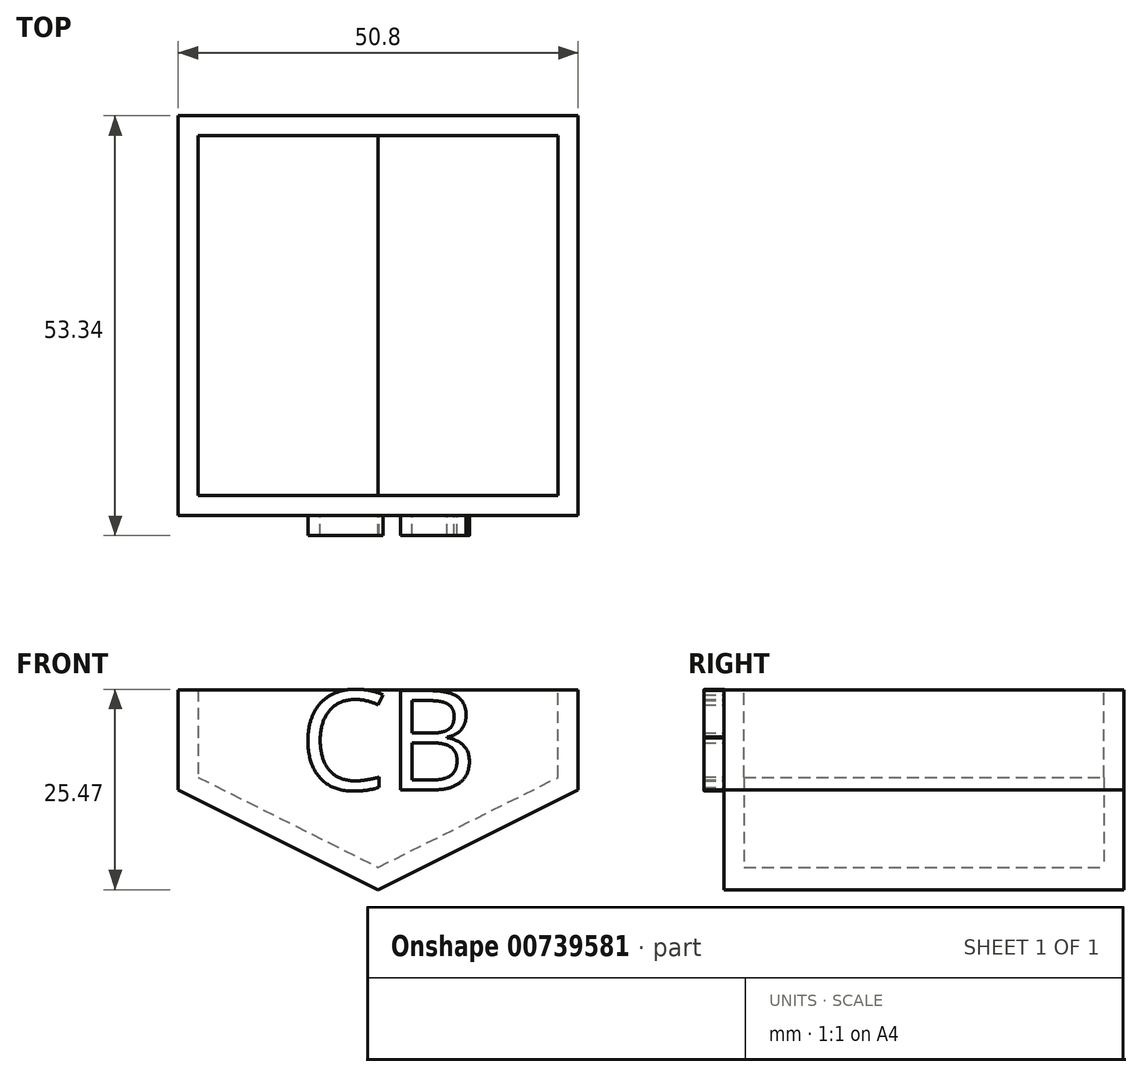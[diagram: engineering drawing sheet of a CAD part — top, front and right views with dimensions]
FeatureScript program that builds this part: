
annotation { "Feature Type Name" : "Feature", "Feature Type Description" : "" }
export const myFeature = defineFeature(function(context is Context, id is Id, definition is map)
    precondition{}
    {
        {
            var Q0;
            Q0=qCreatedBy(makeId("Front.planeOp"),FACE);
            var sketch = newSketch(context, id + "F0", { "sketchPlane" : qUnion([Q0])});
            skLineSegment(sketch, "E0", {"start": v(25.4, 0) * mm, "end": v(25.4, 12.7) * mm});
            skLineSegment(sketch, "E1", {"start": v(25.4, 12.7) * mm, "end": v(-25.4, 12.7) * mm});
            skLineSegment(sketch, "E2", {"start": v(-25.4, 12.7) * mm, "end": v(-25.4, 0) * mm});
            skLineSegment(sketch, "E3", {"start": v(0, 12.7) * mm, "end": v(0, -12.7) * mm});
            skLineSegment(sketch, "E4", {"start": v(0, -12.7) * mm, "end": v(25.4, 0) * mm});
            skLineSegment(sketch, "E5", {"start": v(-25.4, 0) * mm, "end": v(0, -12.7) * mm});
            skSolve(sketch);
        }
        {
            var Q0;
            Q0 = qSketchRegion(id + "F0", true);
            extrude(context, id + "F1", {"entities" : qUnion([Q0]), "depth" : 50.8 * mm, "offsetDistance" : 25.4 * mm});
        }
        {
            var Q0;
            Q0=makeQuery(id+"F1.opExtrude","SWEPT_FACE",FACE,{"disambiguationData":[OSD([sQuery(id+"F0.wireOp",EDGE,"E1")])]});
            shell(context, id + "F2", {"entities" : qUnion([Q0]), "thickness" : 2.54 * mm});
        }
        {
            var Q0;
            Q0=makeQuery(id+"F1.opExtrude","CAP_FACE",FACE,{"disambiguationData":[OSD([sQuery(id+"F0.wireOp",EDGE,"E0"),sQuery(id+"F0.wireOp",EDGE,"E1"),sQuery(id+"F0.wireOp",EDGE,"E2"),sQuery(id+"F0.wireOp",EDGE,"E4"),sQuery(id+"F0.wireOp",EDGE,"E5")])],"isStart":false});
            var sketch = newSketch(context, id + "F3", { "sketchPlane" : qUnion([Q0])});
            skText(sketch, "E6", { "text": "CB", "fontName": "OpenSans-Regular.ttf"});
            const initialGuessF3  = {"E6": [-0.01, 0, 1, 0, 0.0127]};
            skSetInitialGuess(sketch, initialGuessF3);
            skSolve(sketch);
        }
        {
            var Q0;
            Q0 = qSketchRegion(id + "F3", true);
            extrude(context, id + "F4", {"entities" : qUnion([Q0]), "operationType" : NewBodyOperationType.ADD, "depth" : 2.54 * mm, "offsetDistance" : 25.4 * mm});
        }
    });
